# Revit family: Table-Casual-Naughtone-Fold_Circular
name_source: partatom
category: Furniture
revit_build: Autodesk Revit 2015 (Build: 20150704_0715(x64)
units: mm (PartAtom-declared; Revit-internal decimal feet)

## types (3) — shared parameters
AdditionalMaterials = Additional material and finish options available. Please contact Naughtone direct for further information.
Assembly Code = E2020
AssetType = Movable
BIMObjectName = Table-Casual-Naughtone-Fold_Circular
BarCode = 0.000000
Category = 40.50.21.22 : Dining Tables
CodePerformance = FISP Certified; ISO14001 Certified
Color = White
ComponentDescription = Strong and elegant, fold tables and benches proovide a simple surface with maximum clearance for legs, chairs and fresh air to fit underneath!
Constituents = Wood Top; Steel frame
Description = Fold Circular Table
DurationUnit = Years
ExpectedLife = 15-20
Finish = Polyster powder coat; various top finishes available
Keynote = 40.50.21.22
Manufacturer = Naughtone
ManufacturerAddressUK = 201 Pannal Business Park, Station Road, Harrogate, HG3 1JL
Material = Timber; folded mild steel frame
ModelReference = Fold Circular Table
NBSReference = 40.50.21.22
NominalHeight = 750 mm  [stored 2.46063 ft]
Product URL = http://www.naughtone.com
ProductInformation = http://www.naughtone.com
ReplacementCost = 0.00
SerialNumber = 0.000000
Shape = Circular
SustainabilityPerformance = 55.3% reusable content. 72% recycled & recyclable content
TagNumber = 0.000000
TypeName = Table-Casual-Naughtone-Fold_Circular
URL = http://www.naughtone.com
Uniclass2015 = 40.50.21.22
Version = 1
WarrantyDescription = 5 year warranty
WarrantyDurationLabor = 5
WarrantyDurationParts = 5
WarrantyDurationUnit = Years
_current revision = 1
_distributed by = www.bimbox.co.uk
zero-valued in all types: Cost, _BIMspec_GUID

## per-type parameters (varying)
| type | AssetIdentifier | Model | ModelNumber | Name | NominalLength | NominalWidth | Type Comments |
| 1600mmx1600mmx750mm | FOLD-1600-DIA | FOLD-1600-DIA | FOLD-1600-DIA | 1600mmx1600mmx750mm, Fold Circular Table | 1600 mm  [stored 5.24934 ft] | 1600 mm  [stored 5.24934 ft] | 1600x1600x750 |
| 1200mmx1200mmx750mm | FOLD-1200-DIA | FOLD-1200-DIA | FOLD-1200-DIA | 1200mmx1200mmx750mm, Fold Circular Table | 1200 mm | 1200 mm | 1200x1200x750 |
| 1400mmx1400mmx750mm | FOLD-1400-DIA | FOLD-1400-DIA | FOLD-1400-DIA | 1400mmx1400mmx750mm, Fold Circular Table | 1400 mm  [stored 4.59318 ft] | 1400 mm  [stored 4.59318 ft] | 1400x1400x750 |

note: column(s) folded — value = type name in every type: Size

note: [stored X ft] marks values corroborated as IEEE doubles in the binary element streams (Revit-internal decimal feet)

## geometry (parser evidence)
native form markers: Sweep x6
no freeform markers — native parametric forms only
